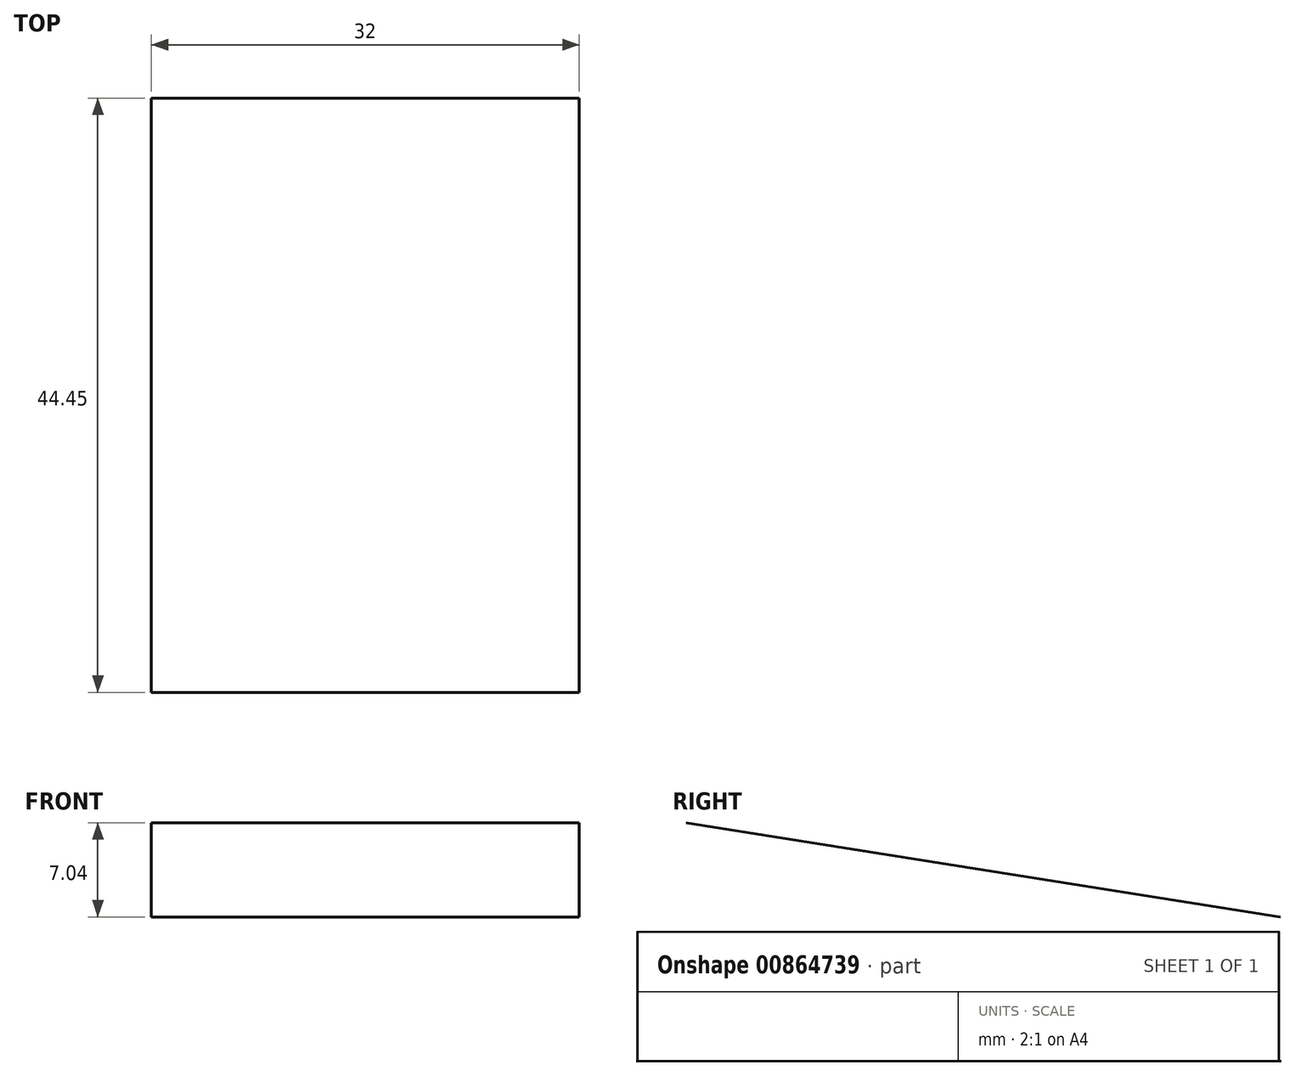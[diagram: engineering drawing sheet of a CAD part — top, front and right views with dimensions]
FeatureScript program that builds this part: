
annotation { "Feature Type Name" : "Feature", "Feature Type Description" : "" }
export const myFeature = defineFeature(function(context is Context, id is Id, definition is map)
    precondition{}
    {
        {
            var Q0;
            Q0=qCreatedBy(makeId("Right.planeOp"),FACE);
            var sketch = newSketch(context, id + "F0", { "sketchPlane" : qUnion([Q0])});
            skLineSegment(sketch, "E0", {"start": v(13.29, 5.96) * mm, "end": v(-31.16, 13) * mm});
            skSolve(sketch);
        }
        {
            var Q0;
            Q0=sQuery(id+"F0.wireOp",EDGE,"E0");
            extrude(context, id + "F1", {"bodyType" : ToolBodyType.SURFACE, "surfaceEntities" : qUnion([Q0]), "endBound" : BoundingType.SYMMETRIC, "depth" : 32 * mm, "offsetDistance" : 25.4 * mm});
        }
    });
